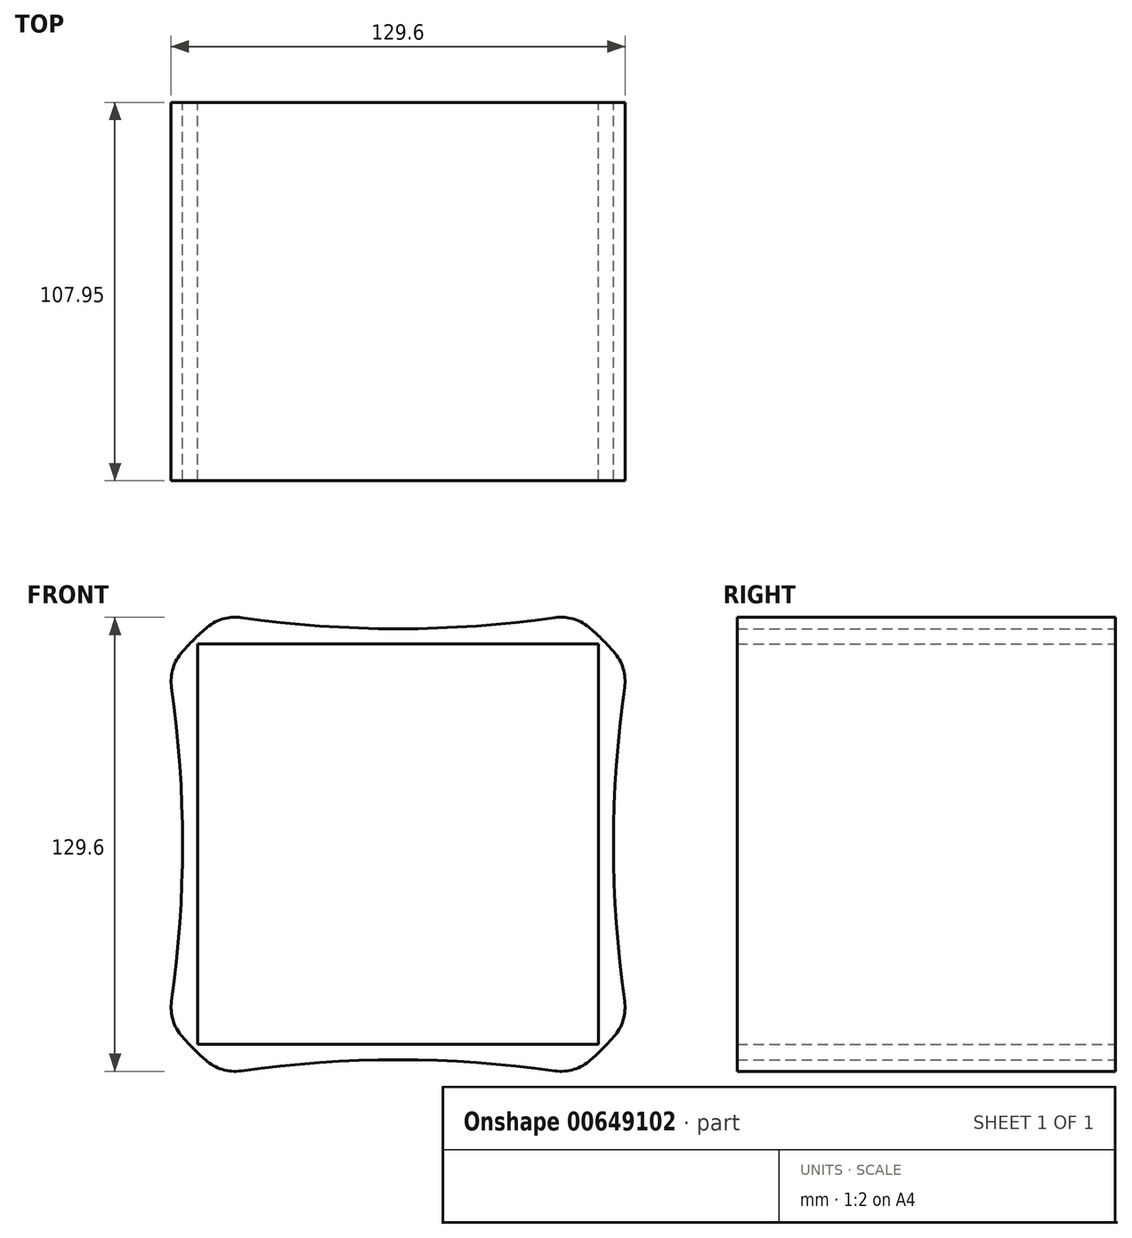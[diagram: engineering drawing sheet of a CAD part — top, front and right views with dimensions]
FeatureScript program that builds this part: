
annotation { "Feature Type Name" : "Feature", "Feature Type Description" : "" }
export const myFeature = defineFeature(function(context is Context, id is Id, definition is map)
    precondition{}
    {
        {
            var Q0;
            Q0=qCreatedBy(makeId("Front.planeOp"),FACE);
            var sketch = newSketch(context, id + "F0", { "sketchPlane" : qUnion([Q0])});
            skArc(sketch, "E0", {"start": v(-50.24, 65.5) * mm, "mid": v(-58.37, 58.37) * mm, "end": v(-65.5, 50.24) * mm});
            skArc(sketch, "E1", {"start": v(-50.24, 65.5) * mm, "mid": v(0, 61.53) * mm, "end": v(50.24, 65.5) * mm});
            skLineSegment(sketch, "E2", {"start": v(-117.82, 0) * mm, "end": v(116.73, 0) * mm, "construction": true});
            skLineSegment(sketch, "E3", {"start": v(0, 89.36) * mm, "end": v(0, -102.08) * mm, "construction": true});
            skArc(sketch, "E4.MirrorCS", {"start": v(50.24, 65.5) * mm, "mid": v(0, 61.53) * mm, "end": v(-50.24, 65.5) * mm});
            skArc(sketch, "E5.MirrorCS", {"start": v(50.24, -65.5) * mm, "mid": v(0, -61.53) * mm, "end": v(-50.24, -65.5) * mm});
            skArc(sketch, "E6.1.0", {"start": v(65.5, -50.24) * mm, "mid": v(61.53, 0) * mm, "end": v(65.5, 50.24) * mm});
            skArc(sketch, "E6.1.1", {"start": v(-65.5, -50.24) * mm, "mid": v(-61.53, 0) * mm, "end": v(-65.5, 50.24) * mm});
            skArc(sketch, "E6.2.0", {"start": v(-50.24, -65.5) * mm, "mid": v(0, -61.53) * mm, "end": v(50.24, -65.5) * mm});
            skLineSegment(sketch, "E6.anchor1", {"start": v(0, 0) * mm, "end": v(0, -380.7) * mm, "construction": true});
            skLineSegment(sketch, "E6.anchor2", {"start": v(0, 0) * mm, "end": v(0, 380.7) * mm, "construction": true});
            skArc(sketch, "E7.trimOffspring", {"start": v(-65.5, -50.24) * mm, "mid": v(-58.37, -58.37) * mm, "end": v(-50.24, -65.5) * mm});
            skArc(sketch, "E8.trimOffspring", {"start": v(65.5, 50.24) * mm, "mid": v(58.37, 58.37) * mm, "end": v(50.24, 65.5) * mm});
            skArc(sketch, "E9.trimOffspring", {"start": v(50.24, -65.5) * mm, "mid": v(58.37, -58.37) * mm, "end": v(65.5, -50.24) * mm});
            skLineSegment(sketch, "E10.bottom", {"start": v(57.15, -57.15) * mm, "end": v(-57.15, -57.15) * mm});
            skLineSegment(sketch, "E10.top", {"start": v(57.15, 57.15) * mm, "end": v(-57.15, 57.15) * mm});
            skLineSegment(sketch, "E10.left", {"start": v(57.15, -57.15) * mm, "end": v(57.15, 57.15) * mm});
            skLineSegment(sketch, "E10.right", {"start": v(-57.15, -57.15) * mm, "end": v(-57.15, 57.15) * mm});
            skSolve(sketch);
        }
        {
            var Q0;
            Q0 = qSketchRegion(id + "F0", true);
            extrude(context, id + "F1", {"entities" : qUnion([Q0]), "depth" : 107.95 * mm, "offsetDistance" : 25.4 * mm});
        }
        {
            var Q0;
            Q0=makeQuery(id+"F1.opExtrude","SWEPT_EDGE",EDGE,{"disambiguationData":[OSD([sQuery(id+"F0.wireOp",EDGE,"E0"),sQuery(id+"F0.wireOp",EDGE,"E6.1.1")])]});
            var Q1;
            Q1=makeQuery(id+"F1.opExtrude","SWEPT_EDGE",EDGE,{"disambiguationData":[OSD([sQuery(id+"F0.wireOp",EDGE,"E0"),sQuery(id+"F0.wireOp",EDGE,"E1")])]});
            var Q2;
            Q2=makeQuery(id+"F1.opExtrude","SWEPT_EDGE",EDGE,{"disambiguationData":[OSD([sQuery(id+"F0.wireOp",EDGE,"E1"),sQuery(id+"F0.wireOp",EDGE,"E8.trimOffspring")])]});
            var Q3;
            Q3=makeQuery(id+"F1.opExtrude","SWEPT_EDGE",EDGE,{"disambiguationData":[OSD([sQuery(id+"F0.wireOp",EDGE,"E6.1.0"),sQuery(id+"F0.wireOp",EDGE,"E8.trimOffspring")])]});
            var Q4;
            Q4=makeQuery(id+"F1.opExtrude","SWEPT_EDGE",EDGE,{"disambiguationData":[OSD([sQuery(id+"F0.wireOp",EDGE,"E6.2.0"),sQuery(id+"F0.wireOp",EDGE,"E9.trimOffspring")])]});
            var Q5;
            Q5=makeQuery(id+"F1.opExtrude","SWEPT_EDGE",EDGE,{"disambiguationData":[OSD([sQuery(id+"F0.wireOp",EDGE,"E6.1.0"),sQuery(id+"F0.wireOp",EDGE,"E9.trimOffspring")])]});
            var Q6;
            Q6=makeQuery(id+"F1.opExtrude","SWEPT_EDGE",EDGE,{"disambiguationData":[OSD([sQuery(id+"F0.wireOp",EDGE,"E6.2.0"),sQuery(id+"F0.wireOp",EDGE,"E7.trimOffspring")])]});
            var Q7;
            Q7=makeQuery(id+"F1.opExtrude","SWEPT_EDGE",EDGE,{"disambiguationData":[OSD([sQuery(id+"F0.wireOp",EDGE,"E6.1.1"),sQuery(id+"F0.wireOp",EDGE,"E7.trimOffspring")])]});
            fillet(context, id + "F2", {"entities" : qUnion([Q0, Q1, Q2, Q3, Q4, Q5, Q6, Q7]), "radius" : 12.7 * mm, "tangentPropagation" : true, "allowEdgeOverflow" : false});
        }
    });
